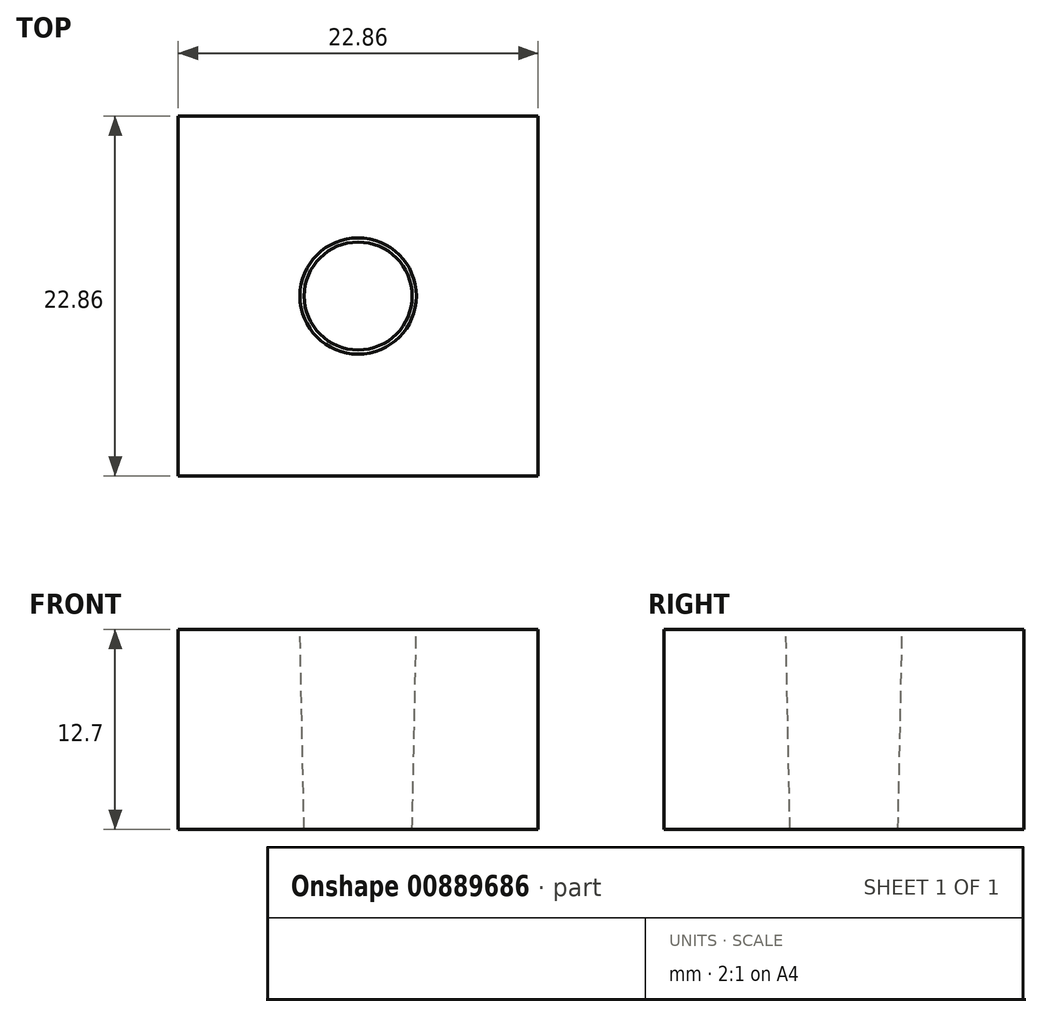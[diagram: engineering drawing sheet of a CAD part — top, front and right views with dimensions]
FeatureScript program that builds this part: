
annotation { "Feature Type Name" : "Feature", "Feature Type Description" : "" }
export const myFeature = defineFeature(function(context is Context, id is Id, definition is map)
    precondition{}
    {
        {
            var Q0;
            Q0=qCreatedBy(makeId("Top.planeOp"),FACE);
            var sketch = newSketch(context, id + "F0", { "sketchPlane" : qUnion([Q0])});
            skLineSegment(sketch, "E0.bottom", {"start": v(11.43, -11.43) * mm, "end": v(-11.43, -11.43) * mm});
            skLineSegment(sketch, "E0.top", {"start": v(11.43, 11.43) * mm, "end": v(-11.43, 11.43) * mm});
            skLineSegment(sketch, "E0.left", {"start": v(11.43, -11.43) * mm, "end": v(11.43, 11.43) * mm});
            skLineSegment(sketch, "E0.right", {"start": v(-11.43, -11.43) * mm, "end": v(-11.43, 11.43) * mm});
            skPoint(sketch, "E0.middle", {"position": v(0, 0) * mm});
            skSolve(sketch);
        }
        {
            var Q0;
            Q0 = qSketchRegion(id + "F0", true);
            extrude(context, id + "F1", {"entities" : qUnion([Q0]), "depth" : 12.7 * mm, "offsetDistance" : 25.4 * mm});
        }
        {
            var Q0;
            Q0=qCreatedBy(makeId("Front.planeOp"),FACE);
            var sketch = newSketch(context, id + "F2", { "sketchPlane" : qUnion([Q0])});
            skLineSegment(sketch, "E1", {"start": v(0, 0) * mm, "end": v(0, 78.74) * mm});
            skLineSegment(sketch, "E2", {"start": v(0, 78.74) * mm, "end": v(5.08, 78.74) * mm});
            skLineSegment(sketch, "E3", {"start": v(0, 0) * mm, "end": v(3.43, 0) * mm});
            skLineSegment(sketch, "E4", {"start": v(3.43, 0) * mm, "end": v(5.08, 78.74) * mm});
            skSolve(sketch);
        }
        {
            var Q0;
            Q0 = qSketchRegion(id + "F2", true);
            var Q1;
            Q1=sQuery(id+"F2.wireOp",EDGE,"E1");
            revolve(context, id + "F3", {"operationType" : NewBodyOperationType.REMOVE, "surfaceOperationType" : NewSurfaceOperationType.NEW, "entities" : qUnion([Q0]), "axis" : qUnion([Q1]), "revolveType" : RevolveType.FULL, "oppositeDirection" : true});
        }
    });
